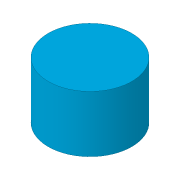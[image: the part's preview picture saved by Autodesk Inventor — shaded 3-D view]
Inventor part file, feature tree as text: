
AUTODESK INVENTOR PART (.ipt)
format: ipt  version: 2017 (Build 210142000, 142)  size: 98,304 bytes
history: native  units: in
note: dims shown in document units (in); Inventor stores cm internally (conversion verified against a paired STEP export)
features: extrude x1, sketch x1
ambient origin geometry x8: Origin, YZ Plane, XZ Plane, XY Plane, X Axis, Y Axis, Z Axis, Center Point
bodies: Solid1 (feature_tree)
feature tree (2):
  extrude  "Extrusion1"  Depth=0.1693in TaperAngle=0.0deg
  sketch  "Sketch1"  dims[d0=0.25in d1=0.1693in d2=0.0in]
